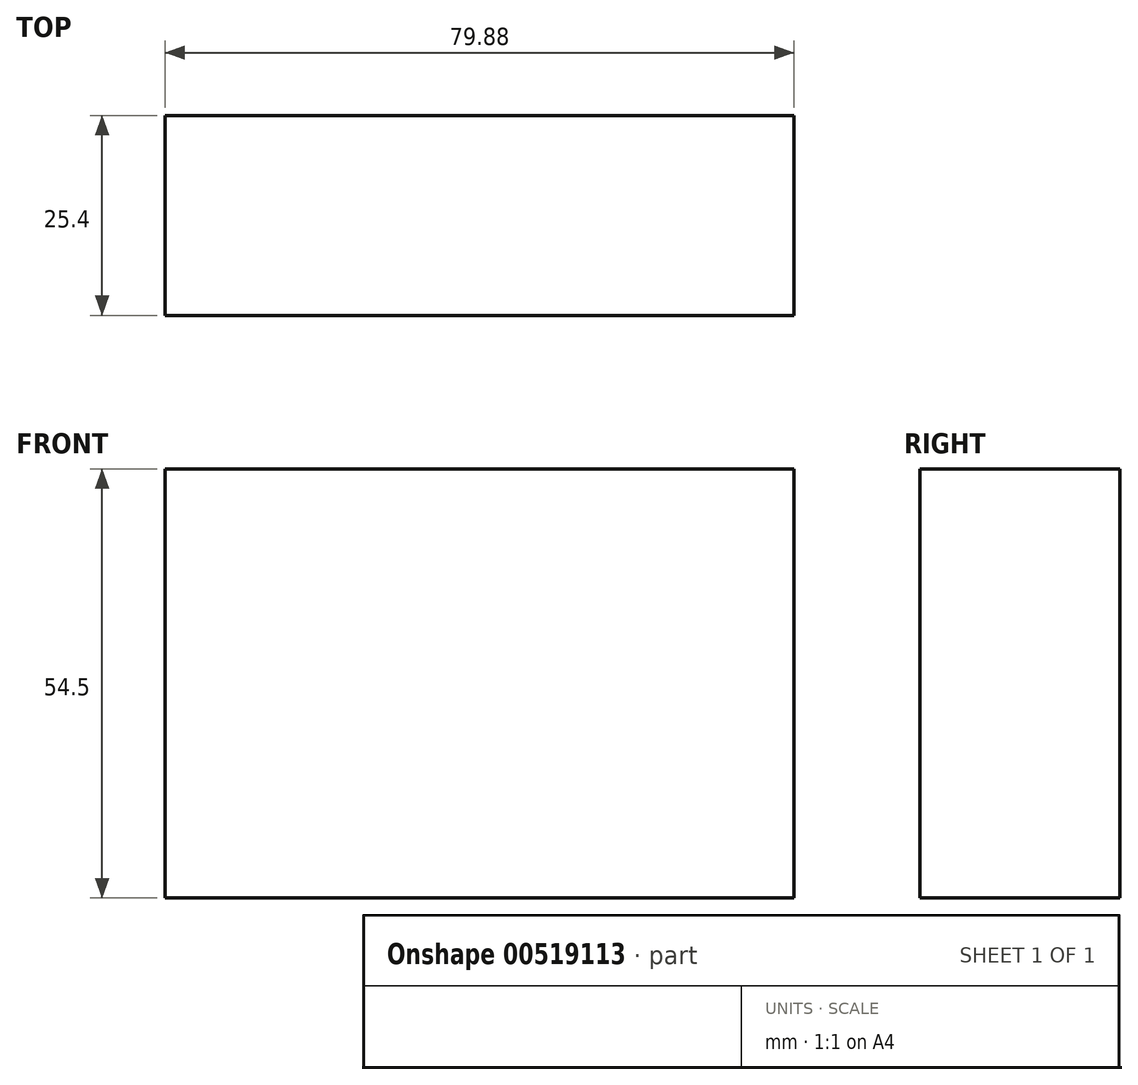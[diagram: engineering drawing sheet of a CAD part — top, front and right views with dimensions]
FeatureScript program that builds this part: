
annotation { "Feature Type Name" : "Feature", "Feature Type Description" : "" }
export const myFeature = defineFeature(function(context is Context, id is Id, definition is map)
    precondition{}
    {
        {
            var Q0;
            Q0=qCreatedBy(makeId("Front.planeOp"),FACE);
            var sketch = newSketch(context, id + "F0", { "sketchPlane" : qUnion([Q0])});
            skLineSegment(sketch, "E0.bottom", {"start": v(-39.94, 27.25) * mm, "end": v(39.94, 27.25) * mm});
            skLineSegment(sketch, "E0.top", {"start": v(-39.94, -27.25) * mm, "end": v(39.94, -27.25) * mm});
            skLineSegment(sketch, "E0.left", {"start": v(-39.94, 27.25) * mm, "end": v(-39.94, -27.25) * mm});
            skLineSegment(sketch, "E0.right", {"start": v(39.94, 27.25) * mm, "end": v(39.94, -27.25) * mm});
            skPoint(sketch, "E0.middle", {"position": v(0, 0) * mm});
            skSolve(sketch);
        }
        {
            var Q0;
            Q0 = qSketchRegion(id + "F0", true);
            extrude(context, id + "F1", {"entities" : qUnion([Q0]), "depth" : 25.4 * mm});
        }
        {
            var Q0;
            Q0=makeQuery(id+"F1.opExtrude","SWEPT_FACE",FACE,{"disambiguationData":[OSD([sQuery(id+"F0.wireOp",EDGE,"E0.bottom")])]});
            var sketch = newSketch(context, id + "F2", { "sketchPlane" : qUnion([Q0])});
            skCircle(sketch, "E1", {"center": v(0, -11.26) * mm, "radius": 9.7 * mm});
            skSolve(sketch);
        }
        {
            var Q0;
            Q0 = qSketchRegion(id + "F2", true);
            extrude(context, id + "F3", {"entities" : qUnion([Q0]), "operationType" : NewBodyOperationType.ADD, "oppositeDirection" : true, "depth" : 25.4 * mm});
        }
    });
